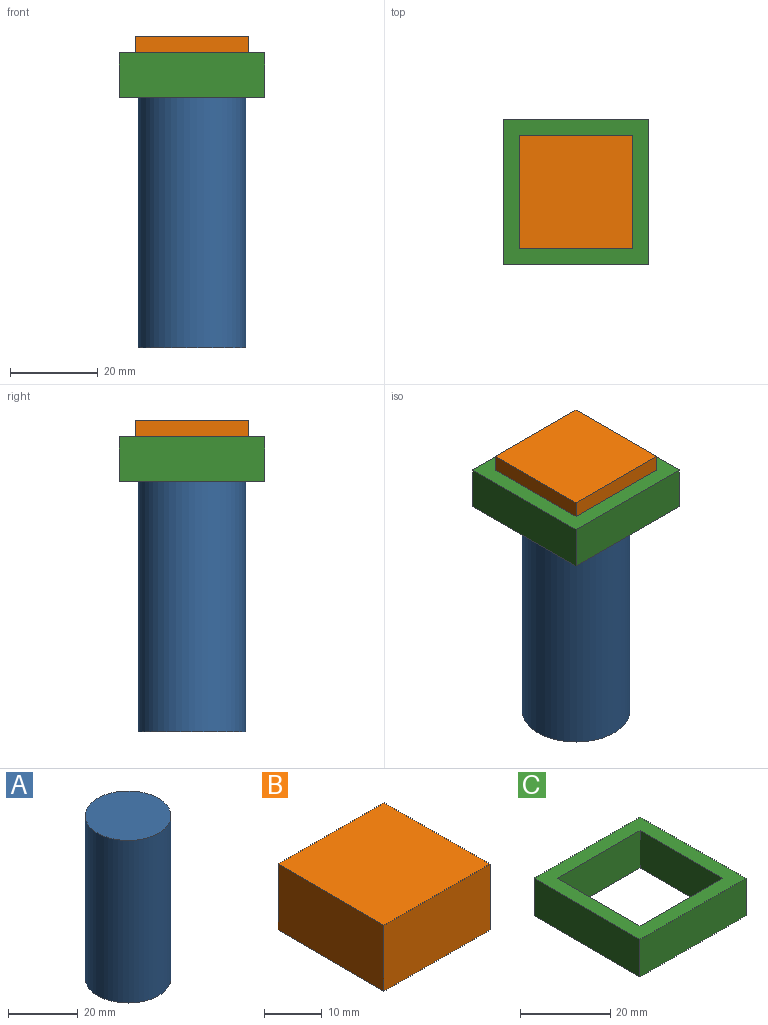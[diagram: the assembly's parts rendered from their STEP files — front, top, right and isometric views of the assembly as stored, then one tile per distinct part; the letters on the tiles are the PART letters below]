
ASSEMBLY  parts=3 mates=2
PART A: 3 faces, bbox 24.6x24.6x57.2 mm
  f0: cylinder r=12.32mm len=57.15mm, axis (0,0,1), area 4423.6mm2, adj f1,f2
  f1: plane 24.64x24.64mm, normal (0,0,-1), area 476.8mm2, adj f0
  f2: plane 24.64x24.64mm, normal (0,0,1), area 476.8mm2, adj f0
PART B: 6 faces, bbox 25.9x25.9x14 mm
  f0: plane 25.91x13.97mm, normal (0,-1,0), area 361.9mm2, adj f1,f3,f4,f5
  f1: plane 25.91x13.97mm, normal (1,0,0), area 361.9mm2, adj f0,f2,f4,f5
  f2: plane 25.91x13.97mm, normal (0,1,0), area 361.9mm2, adj f1,f3,f4,f5
  f3: plane 25.91x13.97mm, normal (-1,0,0), area 361.9mm2, adj f0,f2,f4,f5
  f4: plane 25.91x25.91mm, normal (0,0,1), area 671.2mm2, adj f0,f1,f2,f3
  f5: plane 25.91x25.91mm, normal (0,0,-1), area 671.2mm2, adj f0,f1,f2,f3
PART C: 10 faces, bbox 33.3x33.3x10.2 mm
  f0: plane 33.27x10.16mm, normal (0,-1,0), area 338.1mm2, adj f1,f7,f8,f9
  f1: plane 33.27x10.16mm, normal (1,0,0), area 338.1mm2, adj f0,f2,f8,f9
  f2: plane 33.27x10.16mm, normal (0,1,0), area 338.1mm2, adj f1,f7,f8,f9
  f3: plane 25.91x10.16mm, normal (-1,0,0), area 263.2mm2, adj f4,f6,f8,f9
  f4: plane 25.91x10.16mm, normal (0,1,0), area 263.2mm2, adj f3,f5,f8,f9
  f5: plane 25.91x10.16mm, normal (1,0,0), area 263.2mm2, adj f4,f6,f8,f9
  f6: plane 25.91x10.16mm, normal (0,-1,0), area 263.2mm2, adj f3,f5,f8,f9
  f7: plane 33.27x10.16mm, normal (-1,0,0), area 338.1mm2, adj f0,f2,f8,f9
  f8: plane 33.27x33.27mm, normal (0,0,1), area 435.9mm2, adj f0,f1,f2,f3,f4,f5,f6,f7
  f9: plane 33.27x33.27mm, normal (0,0,-1), area 435.9mm2, adj f0,f1,f2,f3,f4,f5,f6,f7
PLACE A t=(-10.46,-13.69,11.7)mm
PLACE B t=(-10.46,-13.69,11.7)mm
PLACE C t=(-10.46,-13.69,11.7)mm
MATE fastened B.f5 <-> A.f0  axis (0,0,-1) through (-10.46,-13.69,11.7)mm
MATE fastened C.f6 <-> B.f2  axis (0,-1,0) through (-23.41,-0.73,11.7)mm
